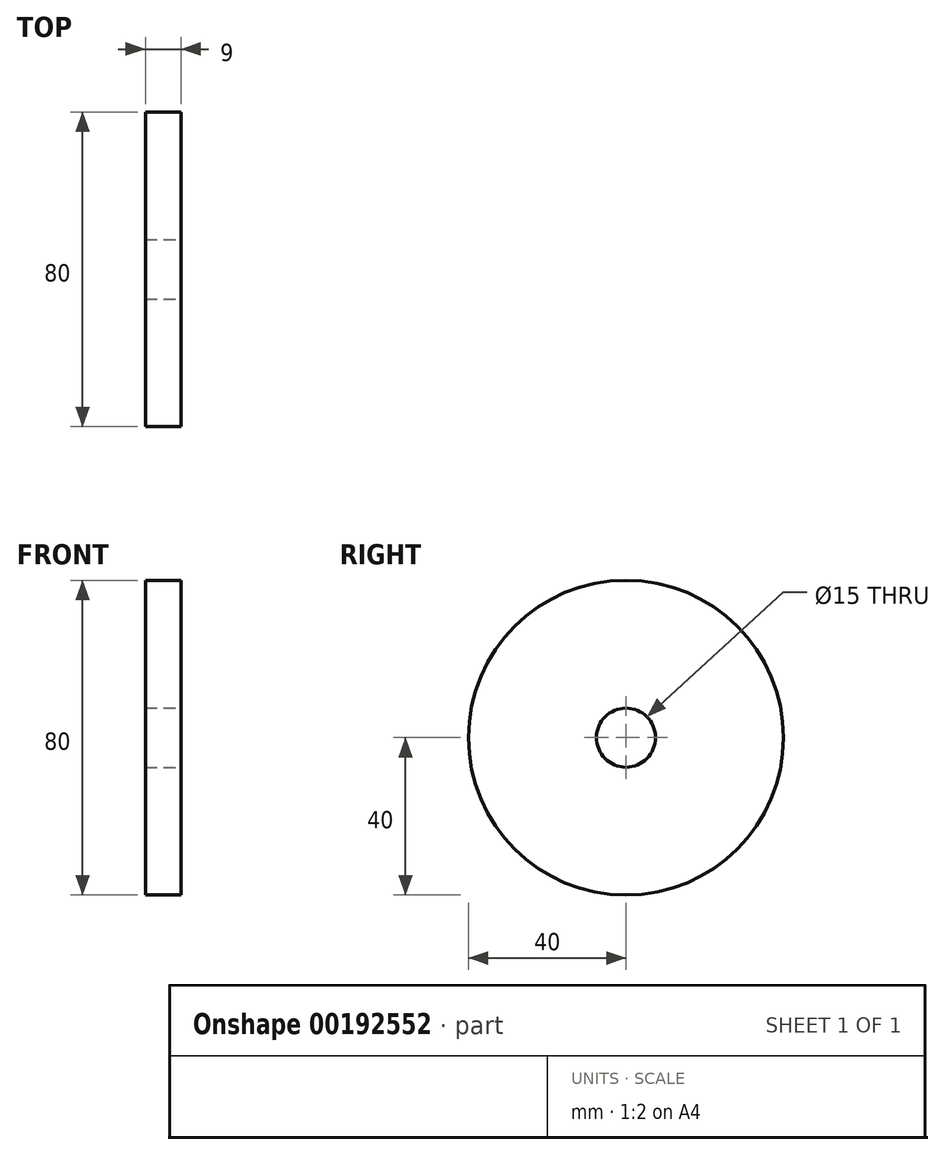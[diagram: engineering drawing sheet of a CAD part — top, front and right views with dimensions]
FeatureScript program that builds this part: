
annotation { "Feature Type Name" : "Feature", "Feature Type Description" : "" }
export const myFeature = defineFeature(function(context is Context, id is Id, definition is map)
    precondition{}
    {
        {
            var Q0;
            Q0=qCreatedBy(makeId("Right.planeOp"),FACE);
            var sketch = newSketch(context, id + "F0", { "sketchPlane" : qUnion([Q0])});
            skCircle(sketch, "E0", {"center": v(0, 0) * mm, "radius": 40 * mm});
            skSolve(sketch);
        }
        {
            var Q0;
            Q0 = qSketchRegion(id + "F0", true);
            extrude(context, id + "F1", {"entities" : qUnion([Q0]), "depth" : 9 * mm});
        }
        {
            var Q0;
            Q0=makeQuery(id+"F1.opExtrude","CAP_FACE",FACE,{"disambiguationData":[OSD([sQuery(id+"F0.wireOp",EDGE,"E0")])],"isStart":false});
            var sketch = newSketch(context, id + "F2", { "sketchPlane" : qUnion([Q0])});
            skCircle(sketch, "E1", {"center": v(0, 0) * mm, "radius": 7.5 * mm});
            skSolve(sketch);
        }
        {
            var Q0;
            Q0 = qSketchRegion(id + "F2", true);
            extrude(context, id + "F3", {"entities" : qUnion([Q0]), "operationType" : NewBodyOperationType.REMOVE, "endBound" : BoundingType.UP_TO_NEXT, "oppositeDirection" : true, "depth" : 25 * mm});
        }
    });
